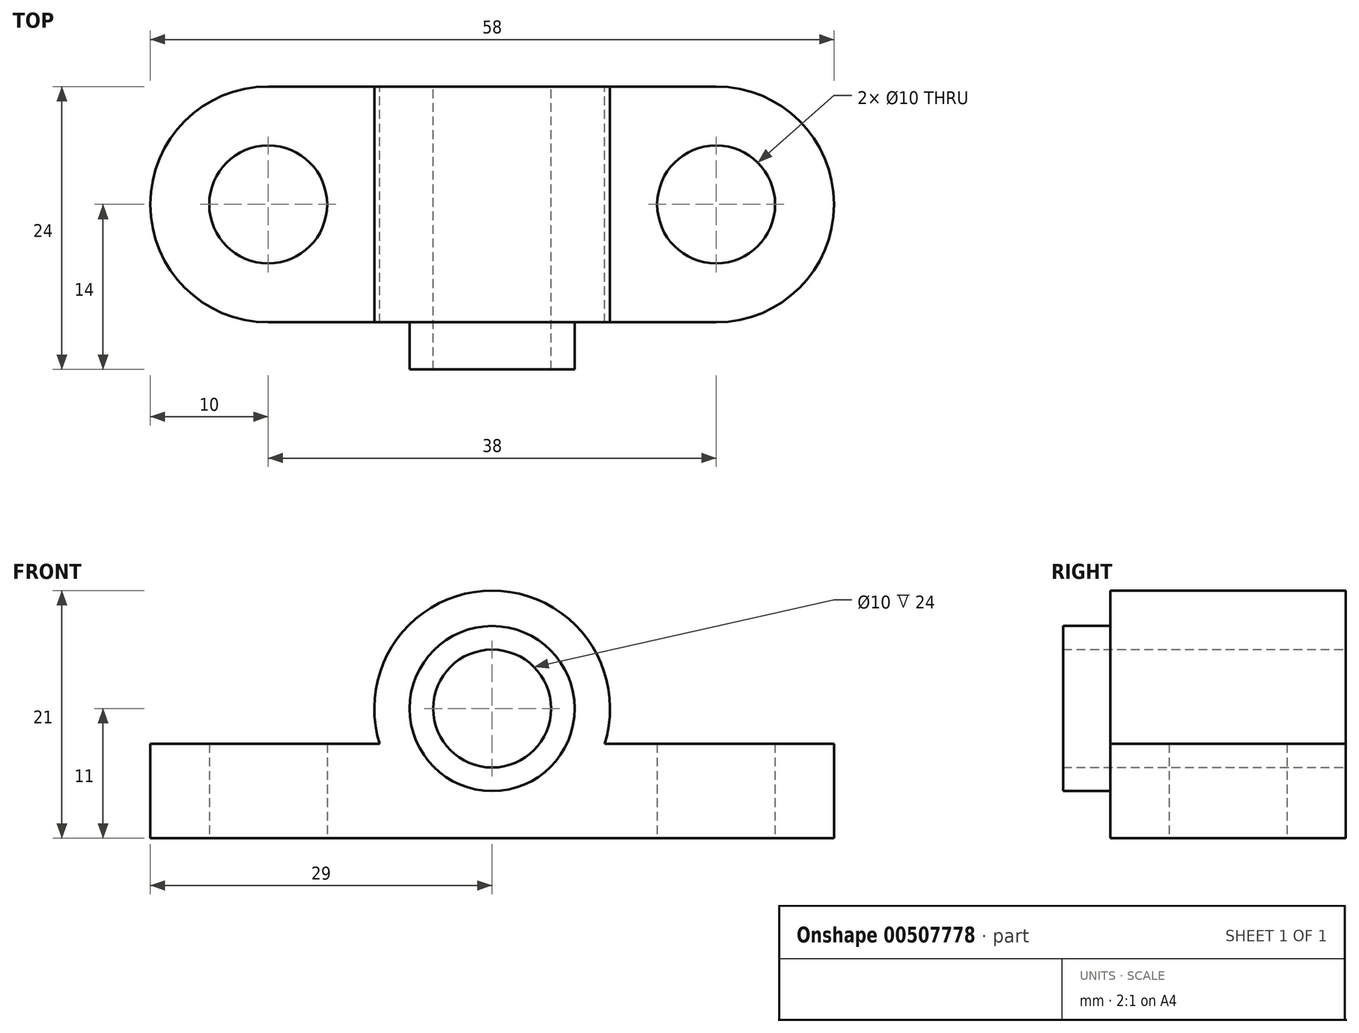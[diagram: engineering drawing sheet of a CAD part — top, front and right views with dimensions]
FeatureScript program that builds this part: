
annotation { "Feature Type Name" : "Feature", "Feature Type Description" : "" }
export const myFeature = defineFeature(function(context is Context, id is Id, definition is map)
    precondition{}
    {
        {
            var Q0;
            Q0=qCreatedBy(makeId("Top.planeOp"),FACE);
            var sketch = newSketch(context, id + "F0", { "sketchPlane" : qUnion([Q0])});
            skLineSegment(sketch, "E0", {"start": v(0, 0) * mm, "end": v(-19, 0) * mm});
            skLineSegment(sketch, "E1", {"start": v(0, 0) * mm, "end": v(0, -20) * mm, "construction": true});
            skLineSegment(sketch, "E2", {"start": v(0, -20) * mm, "end": v(-19, -20) * mm});
            skArc(sketch, "E3", {"start": v(-19, 0) * mm, "mid": v(-29, -10) * mm, "end": v(-19, -20) * mm});
            skCircle(sketch, "E4", {"center": v(-19, -10) * mm, "radius": 5 * mm});
            skLineSegment(sketch, "E5.MirrorCS", {"start": v(0, 0) * mm, "end": v(19, 0) * mm});
            skCircle(sketch, "E6.MirrorC", {"center": v(19, -10) * mm, "radius": 5 * mm});
            skArc(sketch, "E7.MirrorCS", {"start": v(19, 0) * mm, "mid": v(29, -10) * mm, "end": v(19, -20) * mm});
            skLineSegment(sketch, "E8.MirrorCS", {"start": v(0, -20) * mm, "end": v(19, -20) * mm});
            skSolve(sketch);
        }
        {
            var Q0;
            Q0=makeQuery(id+"F0.imprint","IMPRINT",FACE,{"disambiguationData":[TD([[makeQuery(id+"F0.imprint","IMPRINT",EDGE,{"derivedFrom":sQuery(id+"F0.wireOp",EDGE,"E0")}),1.0]])]});
            extrude(context, id + "F1", {"entities" : qUnion([Q0]), "depth" : 8 * mm});
        }
        {
            var Q0;
            Q0=makeQuery(id+"F1.opExtrude","SWEPT_FACE",FACE,{"disambiguationData":[OSD([sQuery(id+"F0.wireOp",EDGE,"E0"),sQuery(id+"F0.wireOp",EDGE,"E5.MirrorCS")])]});
            var sketch = newSketch(context, id + "F2", { "sketchPlane" : qUnion([Q0])});
            skCircle(sketch, "E9", {"center": v(0, 11) * mm, "radius": 5 * mm});
            skCircle(sketch, "E10", {"center": v(0, 11) * mm, "radius": 7 * mm});
            skCircle(sketch, "E11", {"center": v(0, 11) * mm, "radius": 10 * mm});
            skLineSegment(sketch, "E12", {"start": v(10, 11) * mm, "end": v(10, 0) * mm});
            skLineSegment(sketch, "E13", {"start": v(-10, 11) * mm, "end": v(-10, 0) * mm});
            skSolve(sketch);
        }
        {
            var Q0;
            {var subQ0=sQuery(id+"F2.wireOp",EDGE,"E9");var subQ1=makeQuery(id+"F1.opExtrude","CAP_EDGE",EDGE,{"disambiguationData":[OSD([sQuery(id+"F0.wireOp",EDGE,"E0"),sQuery(id+"F0.wireOp",EDGE,"E5.MirrorCS")])],"isStart":false});var subQ2=makeQuery(id+"F2.imprint","INTERSECT",VERTEX,{"disambiguationData":[OD(0.0)],"derivedFrom":[subQ1,subQ0]});Q0=makeQuery(id+"F2.imprint","IMPRINT",FACE,{"disambiguationData":[TD([[makeQuery(id+"F2.imprint","IMPRINT",EDGE,{"disambiguationData":[TD([[subQ2,1.0]])],"derivedFrom":subQ0}),-1.0]])]});}
            var Q1;
            {var subQ0=sQuery(id+"F2.wireOp",EDGE,"E9");var subQ1=makeQuery(id+"F1.opExtrude","CAP_EDGE",EDGE,{"disambiguationData":[OSD([sQuery(id+"F0.wireOp",EDGE,"E0"),sQuery(id+"F0.wireOp",EDGE,"E5.MirrorCS")])],"isStart":false});var subQ2=makeQuery(id+"F2.imprint","INTERSECT",VERTEX,{"disambiguationData":[OD(0.0)],"derivedFrom":[subQ1,subQ0]});Q1=makeQuery(id+"F2.imprint","IMPRINT",FACE,{"disambiguationData":[TD([[makeQuery(id+"F2.imprint","IMPRINT",EDGE,{"disambiguationData":[TD([[subQ2,-1.0]])],"derivedFrom":subQ0}),-1.0]])]});}
            extrude(context, id + "F3", {"entities" : qUnion([Q0, Q1]), "operationType" : NewBodyOperationType.ADD, "oppositeDirection" : true, "depth" : 24 * mm});
        }
        {
            var Q0;
            {var subQ0=sQuery(id+"F2.wireOp",EDGE,"E11");var subQ1=makeQuery(id+"F2.imprint","INTERSECT",VERTEX,{"derivedFrom":[subQ0,sQuery(id+"F2.wireOp",EDGE,"E12")]});Q0=makeQuery(id+"F2.imprint","IMPRINT",FACE,{"disambiguationData":[TD([[makeQuery(id+"F2.imprint","IMPRINT",EDGE,{"disambiguationData":[TD([[subQ1,-1.0]])],"derivedFrom":subQ0}),1.0]])]});}
            extrude(context, id + "F4", {"entities" : qUnion([Q0]), "operationType" : NewBodyOperationType.ADD, "oppositeDirection" : true, "depth" : 20 * mm});
        }
        {
            var Q0;
            Q0=sQuery(id+"F2.wireOp",VERTEX,"E9.center");
            var Q1;
            Q1=makeQuery(id+"F1.opExtrude","SWEPT_BODY",BODY,{"disambiguationData":[OSD([sQuery(id+"F0.wireOp",EDGE,"E0"),sQuery(id+"F0.wireOp",EDGE,"E2"),sQuery(id+"F0.wireOp",EDGE,"E3"),sQuery(id+"F0.wireOp",EDGE,"E4"),sQuery(id+"F0.wireOp",EDGE,"E5.MirrorCS"),sQuery(id+"F0.wireOp",EDGE,"E6.MirrorC"),sQuery(id+"F0.wireOp",EDGE,"E7.MirrorCS"),sQuery(id+"F0.wireOp",EDGE,"E8.MirrorCS")])]});
            hole(context, id + "F5", {"style" : HoleStyle.SIMPLE, "endStyle" : HoleEndStyle.BLIND, "holeDiameter" : 10 * mm, "holeDepth" : 24 * mm, "isTappedThrough" : true, "tappedDepth" : 12 * mm, "tapClearance" : 3, "locations" : qUnion([Q0]), "scope" : qUnion([Q1])});
        }
    });
